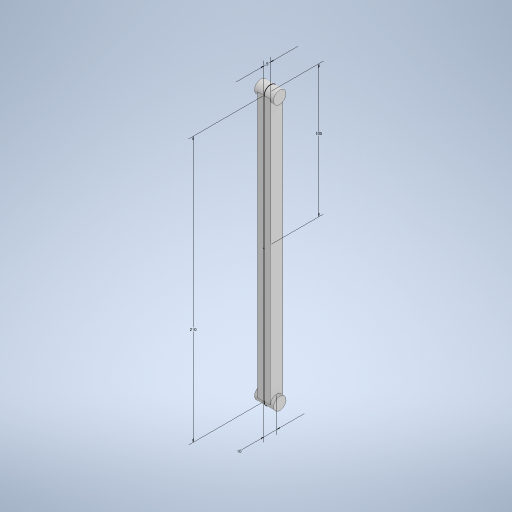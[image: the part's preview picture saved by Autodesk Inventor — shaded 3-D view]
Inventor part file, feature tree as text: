
AUTODESK INVENTOR PART (.ipt)
format: ipt  version: 2024.3 (Build 283343000, 343)  size: 249,344 bytes
history: native  units: mm
features: extrude x2, other x1, sketch x1
ambient origin geometry x8: Origin, YZ Plane, XZ Plane, XY Plane, X Axis, Y Axis, Z Axis, Center Point
bodies: Body1 (feature_tree)
feature tree (4):
  other  "ソリッド1"
  sketch  "スケッチ1"
  extrude  "押し出し1"  Depth=210.0mm
  extrude  "押し出し2"  Depth=10.0mm
